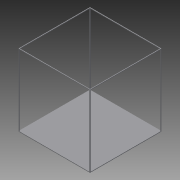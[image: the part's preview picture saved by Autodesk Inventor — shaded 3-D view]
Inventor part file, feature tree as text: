
AUTODESK INVENTOR PART (.ipt)
format: ipt  version: 2014 (Build 180170000, 170)  size: 138,240 bytes
history: native  units: in
note: dims shown in document units (in); Inventor stores cm internally (conversion verified against a paired STEP export)
features: extrude x6, sketch x6
ambient origin geometry x8: Origin, YZ Plane, XZ Plane, XY Plane, X Axis, Y Axis, Z Axis, Center Point
bodies: Solid1 (feature_tree)
feature tree (12):
  extrude  "Extrusion1"  Depth=120.0in
  extrude  "Extrusion2"  Depth=1.0in
  extrude  "Extrusion3"  Depth=1.0in
  extrude  "Extrusion4"  Depth=1.0in
  extrude  "Extrusion5"  Depth=1.0in
  extrude  "Extrusion6"  Depth=120.0in TaperAngle=0.0deg
  sketch  "Sketch1"  dims[d0=120.0in d1=120.0in]
  sketch  "Sketch2"  dims[d2=1.0in d3=0.0in d4=1.0in]
  sketch  "Sketch3"  dims[d5=1.0in d6=1.0in]
  sketch  "Sketch4"  dims[d7=1.0in d8=1.0in]
  sketch  "Sketch5"  dims[d9=1.0in d10=1.0in]
  sketch  "Sketch6"  dims[d11=1.0in d12=120.0in d13=0.0in d14=1.0in d15=1.0in d16=0.0in d17=120.0in d18=1.0in d19=1.0in d20=0.0in d21=120.0in d22=1.0in d23=1.0in d24=0.0in d25=120.0in d26=1.0in d27=1.0in d28=0.0in]
